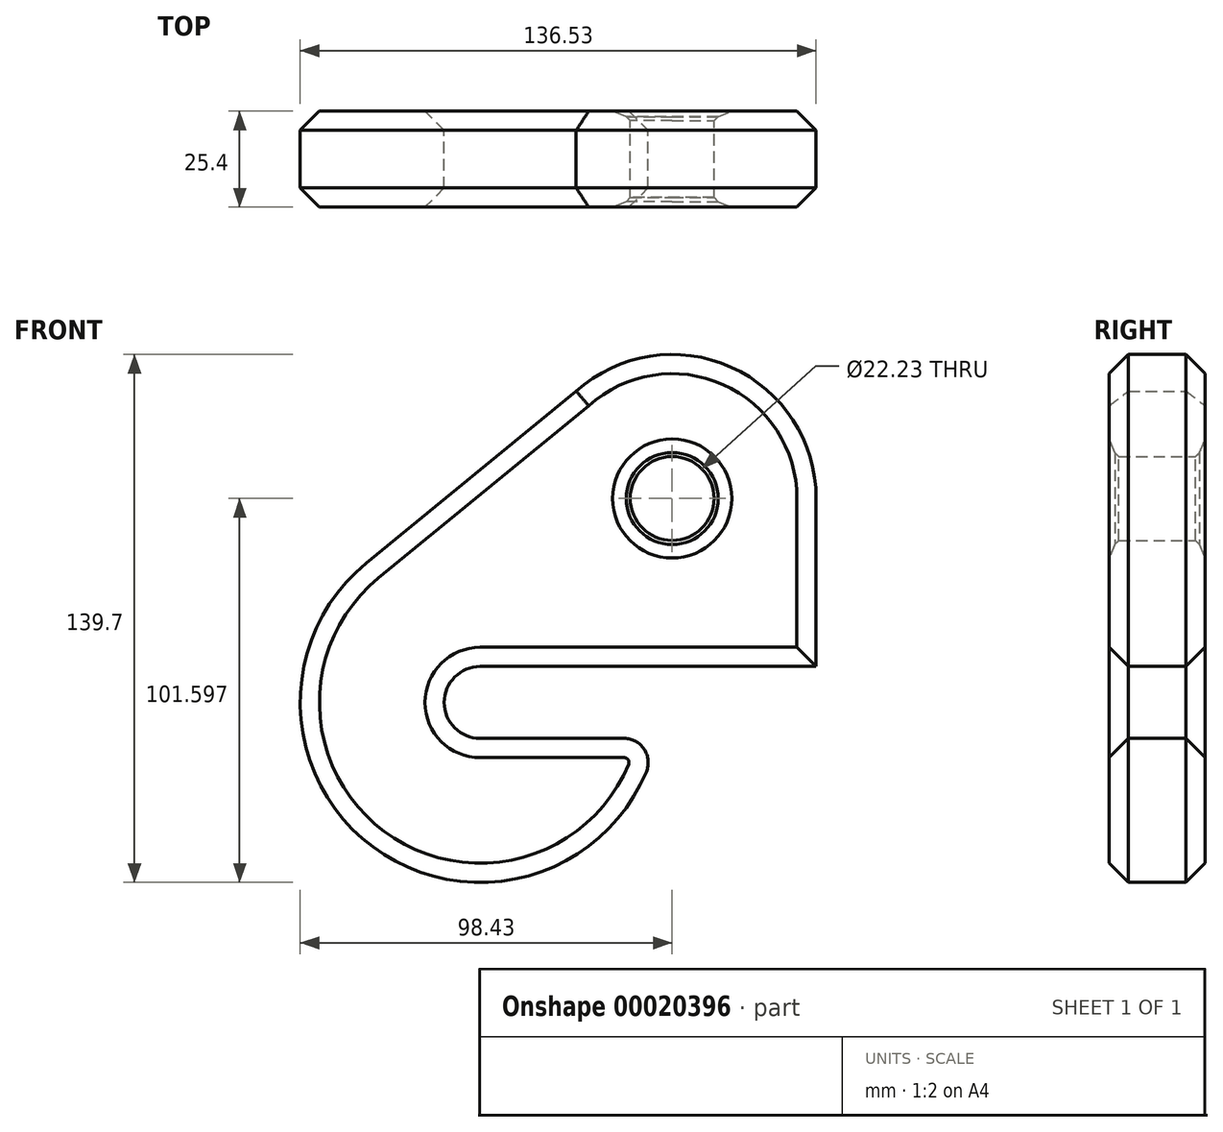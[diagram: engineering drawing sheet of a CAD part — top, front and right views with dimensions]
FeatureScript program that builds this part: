
annotation { "Feature Type Name" : "Feature", "Feature Type Description" : "" }
export const myFeature = defineFeature(function(context is Context, id is Id, definition is map)
    precondition{}
    {
        {
            var Q0;
            Q0=qCreatedBy(makeId("Front.planeOp"),FACE);
            var sketch = newSketch(context, id + "F0", { "sketchPlane" : qUnion([Q0])});
            skPoint(sketch, "E0.rect.middle", {"position": v(0, 0) * mm});
            skArc(sketch, "E1", {"start": v(63.5, 26.99) * mm, "mid": v(40.95, 61.77) * mm, "end": v(0, 55.39) * mm});
            skArc(sketch, "E2", {"start": v(-55.58, 9.85) * mm, "mid": v(-53.83, -65.2) * mm, "end": v(18.56, -45.3) * mm});
            skPoint(sketch, "E3.orphan", {"position": v(-25.4, 26.99) * mm});
            skPoint(sketch, "E0.rect.top.start.orphan", {"position": v(25.4, -26.99) * mm});
            skArc(sketch, "E4", {"start": v(-25.4, -17.46) * mm, "mid": v(-34.93, -26.99) * mm, "end": v(-25.4, -36.51) * mm});
            skCircle(sketch, "E5", {"center": v(25.4, 26.99) * mm, "radius": 11.11 * mm});
            skLineSegment(sketch, "E6.top", {"start": v(63.5, -17.46) * mm, "end": v(-25.4, -17.46) * mm});
            skLineSegment(sketch, "E7", {"start": v(-25.4, -36.51) * mm, "end": v(12.7, -36.51) * mm});
            skPoint(sketch, "E8.visualSharp", {"position": v(21.26, -36.51) * mm});
            skArc(sketch, "E8.filletArc", {"start": v(18.56, -45.3) * mm, "mid": v(17.98, -39.34) * mm, "end": v(12.7, -36.51) * mm});
            skPoint(sketch, "E9.orphan", {"position": v(0, 55.39) * mm});
            skLineSegment(sketch, "E10", {"start": v(0, 55.39) * mm, "end": v(-55.58, 9.85) * mm});
            skLineSegment(sketch, "E11.left", {"start": v(63.5, 26.99) * mm, "end": v(63.5, -17.46) * mm});
            skSolve(sketch);
        }
        {
            var Q0;
            Q0=makeQuery(id+"F0.imprint","IMPRINT",FACE,{"disambiguationData":[TD([[makeQuery(id+"F0.imprint","IMPRINT",EDGE,{"derivedFrom":sQuery(id+"F0.wireOp",EDGE,"E1")}),1.0]])]});
            extrude(context, id + "F1", {"entities" : qUnion([Q0]), "depth" : 25.4 * mm});
        }
        {
            var Q0;
            Q0=makeQuery(id+"F1.opExtrude","SWEPT_FACE",FACE,{"disambiguationData":[OSD([sQuery(id+"F0.wireOp",EDGE,"E5")])]});
            chamfer(context, id + "F2", {"entities" : qUnion([Q0]), "width" : 2.54 * mm, "tangentPropagation" : true});
        }
        {
            var Q0;
            Q0=makeQuery(id+"F1.opExtrude","CAP_FACE",FACE,{"disambiguationData":[OSD([sQuery(id+"F0.wireOp",EDGE,"E1"),sQuery(id+"F0.wireOp",EDGE,"E2"),sQuery(id+"F0.wireOp",EDGE,"E4"),sQuery(id+"F0.wireOp",EDGE,"E5"),sQuery(id+"F0.wireOp",EDGE,"E6.top"),sQuery(id+"F0.wireOp",EDGE,"E7"),sQuery(id+"F0.wireOp",EDGE,"E8.filletArc"),sQuery(id+"F0.wireOp",EDGE,"E10"),sQuery(id+"F0.wireOp",EDGE,"E11.left")])],"isStart":true});
            var Q1;
            Q1=makeQuery(id+"F1.opExtrude","CAP_FACE",FACE,{"disambiguationData":[OSD([sQuery(id+"F0.wireOp",EDGE,"E1"),sQuery(id+"F0.wireOp",EDGE,"E2"),sQuery(id+"F0.wireOp",EDGE,"E4"),sQuery(id+"F0.wireOp",EDGE,"E5"),sQuery(id+"F0.wireOp",EDGE,"E6.top"),sQuery(id+"F0.wireOp",EDGE,"E7"),sQuery(id+"F0.wireOp",EDGE,"E8.filletArc"),sQuery(id+"F0.wireOp",EDGE,"E10"),sQuery(id+"F0.wireOp",EDGE,"E11.left")])],"isStart":false});
            chamfer(context, id + "F3", {"entities" : qUnion([Q0, Q1]), "width" : 5.08 * mm, "tangentPropagation" : true});
        }
    });
